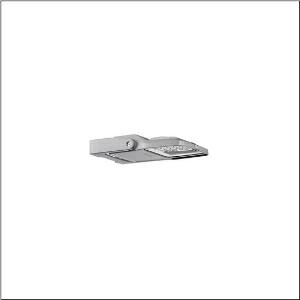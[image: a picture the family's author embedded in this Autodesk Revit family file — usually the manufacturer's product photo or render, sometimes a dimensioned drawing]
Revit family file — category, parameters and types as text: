
# Revit family: floodlight_fl_21_iq_micro___pl64_5xa7762a4e2a_da81
name_source: partatom
category: Lighting Fixtures
units: mm (PartAtom-declared; Revit-internal decimal feet)

## family parameters
Cut with Voids When Loaded = No
Host = Face
Light Source = No
Part Type = Normal
Room Calculation Point = No
Round Connector Dimension = Use Diameter
Shared = No

## types (1)
- --- (1 x LED, 2980 lm, 23.1 W, 4000K)
    Apparent Load = 23 VA
    CIE Flux Codes = 28 80 98 100 100
    Color Rendering = 70
    Color Temperature = 4000K
    Default Elevation = 1800 mm
    Description = Floodlight FL 21 iQ micro, floodlight, primary light control with lens, of PMMA, primary optical cover: protective disc, of toughened safety glass, transparent, light distribution: PL64, light emission: direct distribution, installation type: surface-mounted, LED, High Power LED, rated luminous flux: 2.980lm, luminous efficacy: 129lm/W, light colour: 740, colour temperature: 4000K, control: Auto-Match, Temp-Guard, Night-Set, Smart-Wire, Desk-Remote (wireless, voltage-free reading and setting of iQ features in the workshop via application-optimized NFC function/RFID function), optimised constant luminous flux control (CLO 2.0), Street-Remote, with terminal, 6-pole, mains connection: 220..240V, AC, 50/60Hz, start of lifetime: 23W, end of service life: 24W, reduction: 11W, luminaire housing, of diecast aluminium, powder-coated, Siteco® metallic grey (DB 702S), corrosivity category C5 mid according to DIN EN ISO 12944, sealing non-destructively replaceable, design bracket, of diecast aluminium, powder-coated, Siteco® metallic grey (DB 702S), protection rating (complete): IP66, insulation class (complete): insulation class II (safety insulation), certification: CE, ENEC, VDE, protection symbol: D, impact resistance: IK07, permissible operating ambient temperature: -40..+40°C, permissible operating ambient temperature for outdoor applications: -40..+50°C, standard: DIN EN 12944, LABS conformity tested according to VDMA 24364:2018-05, packaging unit: 1 piece

Light Distribution: PL64
    Height = 65 mm
    Lamp = 1 x LED
    Lamp Light Flux = 2980 lm
    Lamp Power = 23.1 W
    Lamp count = 1
    Length = 312 mm
    Luminous efficacy = 129 lm/W
    Manufacturer = Siteco
    ModVariant = No
    Model = 5XA7762A4E2A
    Mounting Place = Wall
    Mounting Type = Surface mounted
    Number of Poles = 1
    OnlyDefault = Yes
    Power Factor = 1
    Product Name = Floodlight FL 21 iQ micro | PL64
    Product group = floodlight | wall mounted
    ProductGroupID = 2001
    Protection Class = Protection class II
    Protection Degree = IP 66
    RLX_Detail_Level = 1
    RLX_Emergency_Light_Flux = 0 lm
    RLX_Emergency_Type = 0
    RLX_Emergency_Type_DB = No
    RlxData = <blob elided: 97317 chars, md5=62b29e16>
    Socket = socket
    Standby Power = 0 W
    System Light Flux = 2980 lm
    System Power = 23 W
    Type Comments = factory setting: luminous flux: 100 % | dim-lin: 254 | 455 mA
    Type Image = l_1006878.jpg
    URL = http://relux.com
    VarID = @adj_131943
    Voltage = 0 V
    Weight = 0.00 kg
    Width = 230 mm

## geometry (parser evidence)
native form markers: Blend x4, Sweep x13
no freeform markers — native parametric forms only
